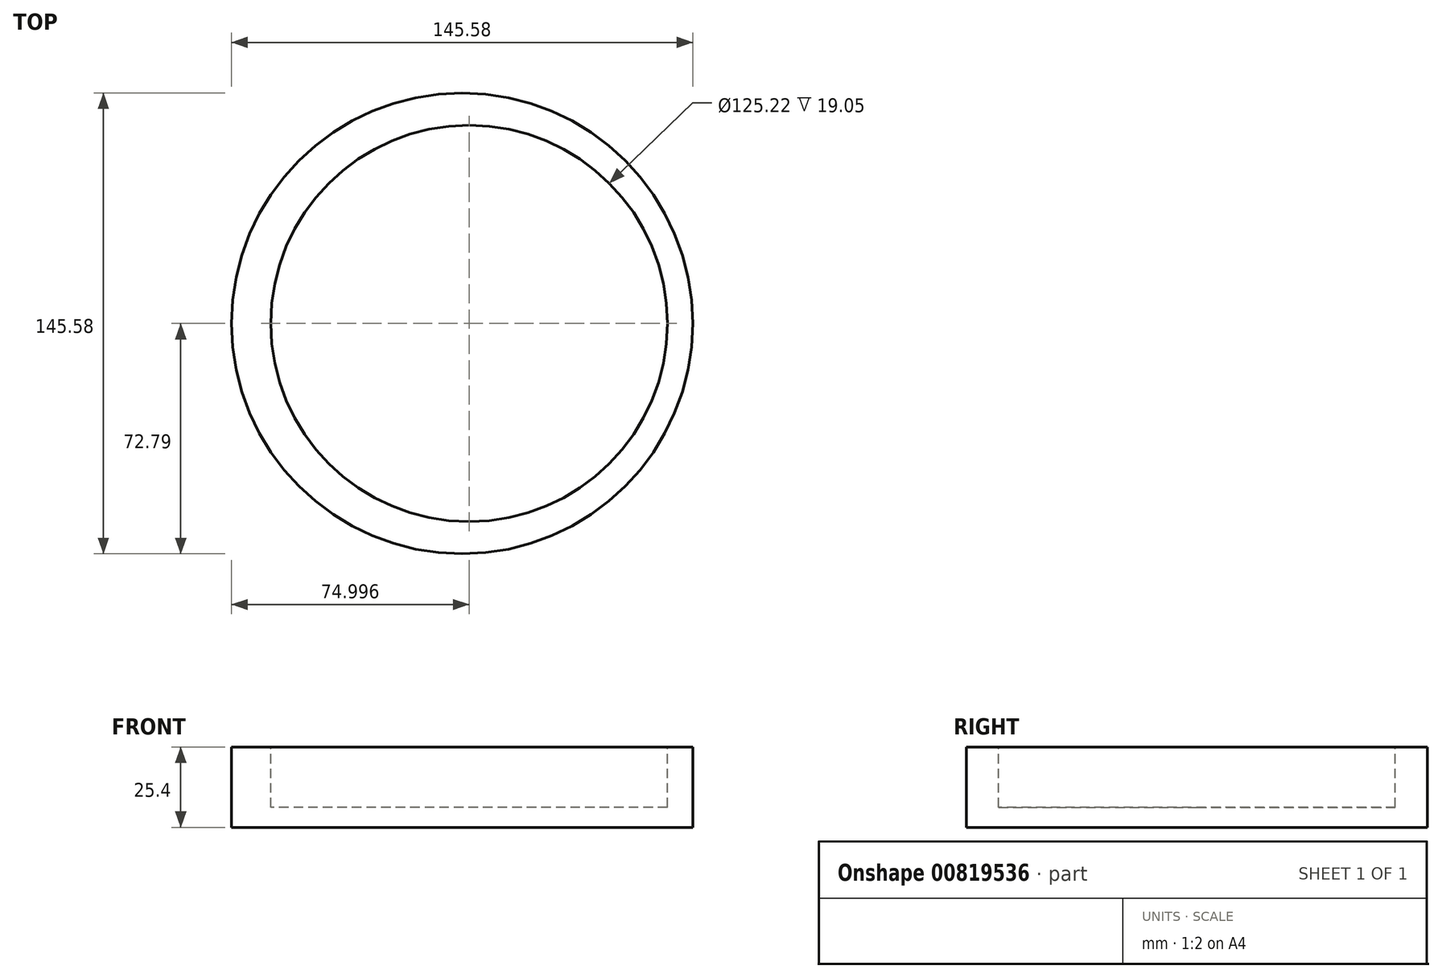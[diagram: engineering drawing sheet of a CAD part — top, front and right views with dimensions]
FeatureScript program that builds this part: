
annotation { "Feature Type Name" : "Feature", "Feature Type Description" : "" }
export const myFeature = defineFeature(function(context is Context, id is Id, definition is map)
    precondition{}
    {
        {
            var Q0;
            Q0=qCreatedBy(makeId("Top.planeOp"),FACE);
            var sketch = newSketch(context, id + "F0", { "sketchPlane" : qUnion([Q0])});
            skCircle(sketch, "E0", {"center": v(0, 0) * mm, "radius": 72.79 * mm});
            skCircle(sketch, "E1", {"center": v(0, 0) * mm, "radius": 56.57 * mm});
            skSolve(sketch);
        }
        {
            var Q0;
            Q0=makeQuery(id+"F0.imprint","IMPRINT",FACE,{"disambiguationData":[TD([[makeQuery(id+"F0.imprint","IMPRINT",EDGE,{"derivedFrom":sQuery(id+"F0.wireOp",EDGE,"E0")}),1.0]])]});
            var Q1;
            Q1=makeQuery(id+"F0.imprint","IMPRINT",FACE,{"disambiguationData":[TD([[makeQuery(id+"F0.imprint","IMPRINT",EDGE,{"derivedFrom":sQuery(id+"F0.wireOp",EDGE,"E1")}),1.0]])]});
            extrude(context, id + "F1", {"entities" : qUnion([Q0, Q1]), "depth" : 25.4 * mm, "offsetDistance" : 25.4 * mm});
        }
        {
            var Q0;
            Q0=makeQuery(id+"F1.opExtrude","CAP_FACE",FACE,{"disambiguationData":[OSD([sQuery(id+"F0.wireOp",EDGE,"E0")])],"isStart":false});
            var sketch = newSketch(context, id + "F2", { "sketchPlane" : qUnion([Q0])});
            skCircle(sketch, "E2", {"center": v(2.2, 0) * mm, "radius": 62.61 * mm});
            skSolve(sketch);
        }
        {
            var Q0;
            Q0 = qSketchRegion(id + "F2", true);
            extrude(context, id + "F3", {"entities" : qUnion([Q0]), "operationType" : NewBodyOperationType.REMOVE, "oppositeDirection" : true, "depth" : 19.05 * mm, "offsetDistance" : 25.4 * mm});
        }
    });
